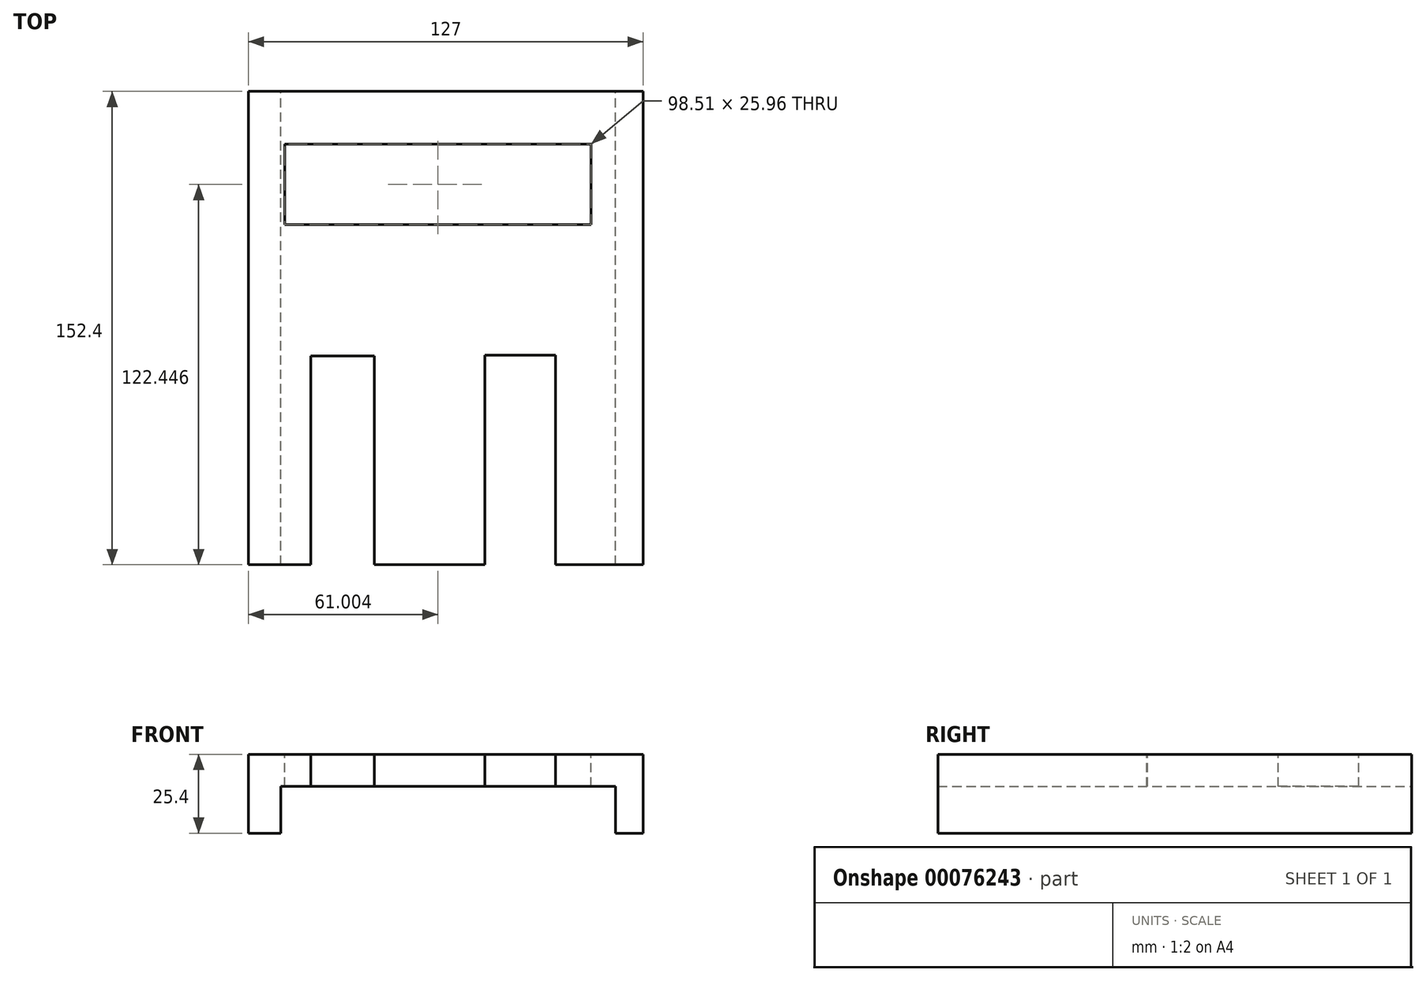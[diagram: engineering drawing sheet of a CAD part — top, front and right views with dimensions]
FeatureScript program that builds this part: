
annotation { "Feature Type Name" : "Feature", "Feature Type Description" : "" }
export const myFeature = defineFeature(function(context is Context, id is Id, definition is map)
    precondition{}
    {
        {
            var Q0;
            Q0=qCreatedBy(makeId("Front.planeOp"),FACE);
            var sketch = newSketch(context, id + "F0", { "sketchPlane" : qUnion([Q0])});
            skLineSegment(sketch, "E0.bottom", {"start": v(-20.04, 25.4) * mm, "end": v(106.96, 25.4) * mm});
            skLineSegment(sketch, "E0.top", {"start": v(-20.04, 0) * mm, "end": v(106.96, 0) * mm});
            skLineSegment(sketch, "E0.left", {"start": v(-20.04, 25.4) * mm, "end": v(-20.04, 0) * mm});
            skLineSegment(sketch, "E0.right", {"start": v(106.96, 25.4) * mm, "end": v(106.96, 0) * mm});
            skSolve(sketch);
        }
        {
            var Q0;
            Q0=makeQuery(id+"F0.imprint","IMPRINT",FACE,{"disambiguationData":[TD([[makeQuery(id+"F0.imprint","IMPRINT",EDGE,{"derivedFrom":sQuery(id+"F0.wireOp",EDGE,"E0.bottom")}),-1.0]])]});
            extrude(context, id + "F1", {"entities" : qUnion([Q0]), "depth" : 152.4 * mm});
        }
        {
            var Q0;
            Q0=qCreatedBy(makeId("Front.planeOp"),FACE);
            var sketch = newSketch(context, id + "F2", { "sketchPlane" : qUnion([Q0])});
            skLineSegment(sketch, "E1.bottom", {"start": v(-9.57, 15.02) * mm, "end": v(98.11, 15.02) * mm});
            skLineSegment(sketch, "E1.top", {"start": v(-9.57, 0) * mm, "end": v(98.11, 0) * mm});
            skLineSegment(sketch, "E1.left", {"start": v(-9.57, 15.02) * mm, "end": v(-9.57, 0) * mm});
            skLineSegment(sketch, "E1.right", {"start": v(98.11, 15.02) * mm, "end": v(98.11, 0) * mm});
            skSolve(sketch);
        }
        {
            var Q0;
            Q0=makeQuery(id+"F2.imprint","IMPRINT",FACE,{"disambiguationData":[TD([[makeQuery(id+"F2.imprint","IMPRINT",EDGE,{"derivedFrom":sQuery(id+"F2.wireOp",EDGE,"E1.bottom")}),-1.0]])]});
            extrude(context, id + "F3", {"entities" : qUnion([Q0]), "operationType" : NewBodyOperationType.REMOVE, "endBound" : BoundingType.THROUGH_ALL, "depth" : 25.4 * mm});
        }
        {
            var Q0;
            Q0=makeQuery(id+"F1.opExtrude","SWEPT_FACE",FACE,{"disambiguationData":[OSD([sQuery(id+"F0.wireOp",EDGE,"E0.right")])]});
            var sketch = newSketch(context, id + "F4", { "sketchPlane" : qUnion([Q0])});
            skCircle(sketch, "E2", {"center": v(-14.9, 8.73) * mm, "radius": 2.38 * mm});
            skSolve(sketch);
        }
        {
            var Q0;
            Q0=makeQuery(id+"F1.opExtrude","SWEPT_FACE",FACE,{"disambiguationData":[OSD([sQuery(id+"F0.wireOp",EDGE,"E0.right")])]});
            var sketch = newSketch(context, id + "F5", { "sketchPlane" : qUnion([Q0])});
            skCircle(sketch, "E3", {"center": v(-133.42, 7.48) * mm, "radius": 3.35 * mm});
            skSolve(sketch);
        }
        {
            var Q0;
            Q0=sQuery(id+"F5.wireOp",EDGE,"E3");
            extrude(context, id + "F6", {"bodyType" : ToolBodyType.SURFACE, "surfaceEntities" : qUnion([Q0]), "endBound" : BoundingType.THROUGH_ALL, "depth" : 25.4 * mm});
        }
        {
            var Q0;
            Q0=makeQuery(id+"F6.opExtrude","SWEPT_BODY",BODY,{"disambiguationData":[OSD([sQuery(id+"F5.wireOp",EDGE,"E3")])]});
            deleteBodies(context, id + "F7", {"entities" : qUnion([Q0])});
        }
        {
            var Q0;
            Q0=makeQuery(id+"F1.opExtrude","SWEPT_FACE",FACE,{"disambiguationData":[OSD([sQuery(id+"F0.wireOp",EDGE,"E0.bottom")])]});
            var sketch = newSketch(context, id + "F8", { "sketchPlane" : qUnion([Q0])});
            skSolve(sketch);
        }
        {
            var Q0;
            {var subQ0=sQuery(id+"F0.wireOp",EDGE,"E0.bottom");Q0=makeQuery(id+"F8.imprint","IMPRINT",FACE,{"disambiguationData":[TD([[makeQuery(id+"F8.imprint","IMPRINT",EDGE,{"derivedFrom":makeQuery(id+"F1.opExtrude","CAP_EDGE",EDGE,{"disambiguationData":[OSD([subQ0])],"isStart":true})}),-1.0]])]});}
            var sketch = newSketch(context, id + "F9", { "sketchPlane" : qUnion([Q0])});
            skLineSegment(sketch, "E4.bottom", {"start": v(0, -152.4) * mm, "end": v(20.47, -152.4) * mm});
            skLineSegment(sketch, "E4.top", {"start": v(0, -85.2) * mm, "end": v(20.47, -85.2) * mm});
            skLineSegment(sketch, "E4.left", {"start": v(0, -152.4) * mm, "end": v(0, -85.2) * mm});
            skLineSegment(sketch, "E4.right", {"start": v(20.47, -152.4) * mm, "end": v(20.47, -85.2) * mm});
            skLineSegment(sketch, "E5.bottom", {"start": v(78.77, -152.4) * mm, "end": v(56.11, -152.4) * mm});
            skLineSegment(sketch, "E5.top", {"start": v(78.77, -84.94) * mm, "end": v(56.11, -84.94) * mm});
            skLineSegment(sketch, "E5.left", {"start": v(78.77, -152.4) * mm, "end": v(78.77, -84.94) * mm});
            skLineSegment(sketch, "E5.right", {"start": v(56.11, -152.4) * mm, "end": v(56.11, -84.94) * mm});
            skSolve(sketch);
        }
        {
            var Q0;
            Q0 = qSketchRegion(id + "F9", true);
            var Q1;
            Q1=makeQuery(id+"F9.imprint","IMPRINT",FACE,{"disambiguationData":[TD([[makeQuery(id+"F9.imprint","IMPRINT",EDGE,{"derivedFrom":sQuery(id+"F9.wireOp",EDGE,"E5.bottom")}),-1.0]])]});
            var Q2;
            Q2=makeQuery(id+"F9.imprint","IMPRINT",FACE,{"disambiguationData":[TD([[makeQuery(id+"F9.imprint","IMPRINT",EDGE,{"derivedFrom":sQuery(id+"F9.wireOp",EDGE,"E4.bottom")}),1.0]])]});
            extrude(context, id + "F10", {"entities" : qUnion([Q0, Q1, Q2]), "operationType" : NewBodyOperationType.REMOVE, "endBound" : BoundingType.THROUGH_ALL, "oppositeDirection" : true, "depth" : 25.4 * mm});
        }
        {
            var Q0;
            {var subQ0=sQuery(id+"F0.wireOp",EDGE,"E0.bottom");Q0=makeQuery(id+"F8.imprint","IMPRINT",FACE,{"disambiguationData":[TD([[makeQuery(id+"F8.imprint","IMPRINT",EDGE,{"derivedFrom":makeQuery(id+"F1.opExtrude","CAP_EDGE",EDGE,{"disambiguationData":[OSD([subQ0])],"isStart":true})}),-1.0]])]});}
            var sketch = newSketch(context, id + "F11", { "sketchPlane" : qUnion([Q0])});
            skLineSegment(sketch, "E6.bottom", {"start": v(90.22, -16.97) * mm, "end": v(-8.3, -16.97) * mm});
            skLineSegment(sketch, "E6.top", {"start": v(90.22, -42.94) * mm, "end": v(-8.3, -42.94) * mm});
            skLineSegment(sketch, "E6.left", {"start": v(90.22, -16.97) * mm, "end": v(90.22, -42.94) * mm});
            skLineSegment(sketch, "E6.right", {"start": v(-8.3, -16.97) * mm, "end": v(-8.3, -42.94) * mm});
            skSolve(sketch);
        }
        {
            var Q0;
            Q0 = qSketchRegion(id + "F11", true);
            extrude(context, id + "F12", {"entities" : qUnion([Q0]), "operationType" : NewBodyOperationType.REMOVE, "endBound" : BoundingType.THROUGH_ALL, "oppositeDirection" : true, "depth" : 25.4 * mm});
        }
    });
